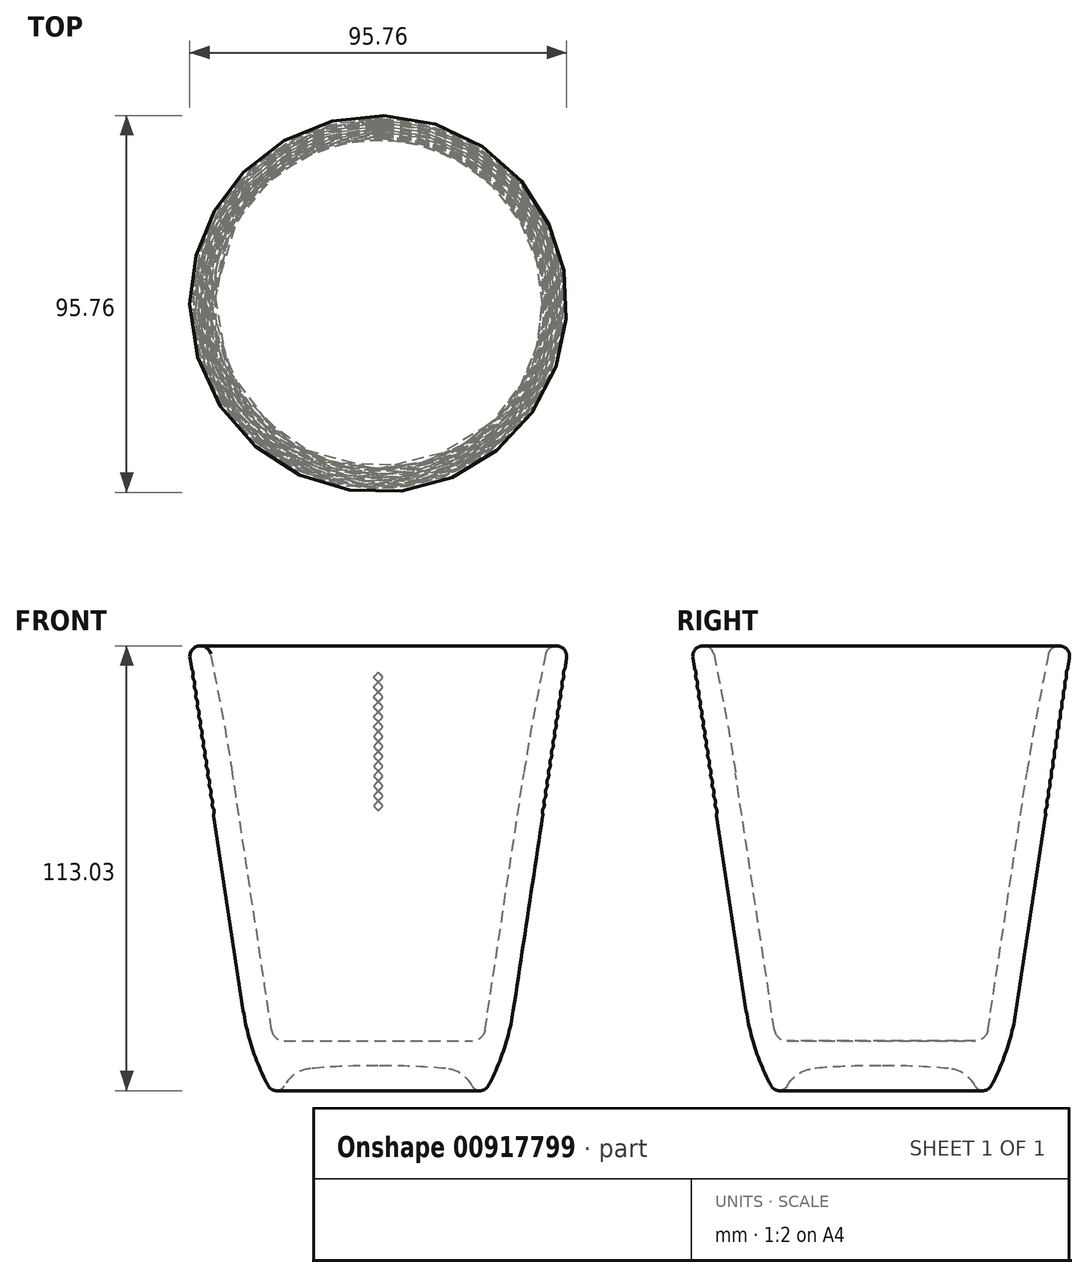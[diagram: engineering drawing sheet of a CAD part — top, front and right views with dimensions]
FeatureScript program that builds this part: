
annotation { "Feature Type Name" : "Feature", "Feature Type Description" : "" }
export const myFeature = defineFeature(function(context is Context, id is Id, definition is map)
    precondition{}
    {
        {
            var Q0;
            Q0=qCreatedBy(makeId("Right.planeOp"),FACE);
            var sketch = newSketch(context, id + "F0", { "sketchPlane" : qUnion([Q0])});
            skLineSegment(sketch, "E0", {"start": v(0, 0) * mm, "end": v(0, 6.35) * mm, "construction": true});
            skArc(sketch, "E1", {"start": v(0, 6.35) * mm, "mid": v(-8.58, 6.17) * mm, "end": v(-17.15, 5.63) * mm});
            skLineSegment(sketch, "E2", {"start": v(-47.85, 109.92) * mm, "end": v(-31.21, 0) * mm});
            skLineSegment(sketch, "E3", {"start": v(-31.21, 0) * mm, "end": v(0, 0) * mm, "construction": true});
            skArc(sketch, "E4", {"start": v(-17.15, 5.63) * mm, "mid": v(-21.07, 4.27) * mm, "end": v(-23.88, 1.2) * mm});
            skArc(sketch, "E5", {"start": v(-27.92, 1.2) * mm, "mid": v(-25.9, 0) * mm, "end": v(-23.88, 1.2) * mm});
            skArc(sketch, "E6", {"start": v(-34.3, 20.32) * mm, "mid": v(-31.93, 10.5) * mm, "end": v(-27.92, 1.2) * mm});
            skLineSegment(sketch, "E7", {"start": v(0, 6.35) * mm, "end": v(0, 12.7) * mm});
            skLineSegment(sketch, "E8", {"start": v(0, 12.7) * mm, "end": v(0, 113.03) * mm, "construction": true});
            skLineSegment(sketch, "E9", {"start": v(0, 12.7) * mm, "end": v(-23.98, 12.7) * mm});
            skArc(sketch, "E10", {"start": v(-27.12, 15.4) * mm, "mid": v(-26.05, 13.47) * mm, "end": v(-23.98, 12.7) * mm});
            skLineSegment(sketch, "E11", {"start": v(-27.12, 15.4) * mm, "end": v(-37, 80.64) * mm});
            skArc(sketch, "E12", {"start": v(-42.54, 110.9) * mm, "mid": v(-45.66, 112.99) * mm, "end": v(-47.85, 109.92) * mm});
            skArc(sketch, "E13", {"start": v(-37, 80.64) * mm, "mid": v(-39.53, 95.81) * mm, "end": v(-42.54, 110.9) * mm});
            skLineSegment(sketch, "E14", {"start": v(-45.18, 113.03) * mm, "end": v(0, 113.03) * mm, "construction": true});
            skLineSegment(sketch, "E15", {"start": v(-47.88, 110.33) * mm, "end": v(-47.88, 115.02) * mm, "construction": true});
            skPoint(sketch, "E16", {"position": v(0, 69.85) * mm});
            skLineSegment(sketch, "E17", {"start": v(-47.85, 109.92) * mm, "end": v(0, 109.92) * mm, "construction": true});
            skSolve(sketch);
        }
        {
            var Q0;
            Q0 = qSketchRegion(id + "F0", true);
            var Q1;
            Q1=sQuery(id+"F0.wireOp",EDGE,"E7");
            revolve(context, id + "F1", {"surfaceOperationType" : NewSurfaceOperationType.NEW, "entities" : qUnion([Q0]), "axis" : qUnion([Q1]), "revolveType" : RevolveType.FULL});
        }
        {
            var Q0;
            Q0=qCreatedBy(makeId("Top.planeOp"),FACE);
            var Q1;
            Q1=sQuery(id+"F0.wireOp",VERTEX,"E16");
            cPlane(context, id + "F2", {"entities" : qUnion([Q0, Q1]), "cplaneType" : CPlaneType.PLANE_POINT, "offset" : 25.4 * mm, "width" : 152.4 * mm, "height" : 152.4 * mm});
        }
        {
            var Q0;
            Q0=qCreatedBy(id+"F2.planeOp",FACE);
            var sketch = newSketch(context, id + "F3", { "sketchPlane" : qUnion([Q0])});
            skCircle(sketch, "E18.cCircle", {"center": v(0, 0) * mm, "radius": 35.98 * mm, "construction": true});
            skLineSegment(sketch, "E18.0", {"start": v(0, 39.94) * mm, "end": v(31.23, 24.9) * mm});
            skLineSegment(sketch, "E18.1", {"start": v(31.23, 24.9) * mm, "end": v(38.94, -8.89) * mm});
            skLineSegment(sketch, "E18.2", {"start": v(38.94, -8.89) * mm, "end": v(17.33, -35.98) * mm});
            skLineSegment(sketch, "E18.3", {"start": v(17.33, -35.98) * mm, "end": v(-17.33, -35.98) * mm});
            skLineSegment(sketch, "E18.4", {"start": v(-17.33, -35.98) * mm, "end": v(-38.94, -8.89) * mm});
            skLineSegment(sketch, "E18.5", {"start": v(-38.94, -8.89) * mm, "end": v(-31.23, 24.9) * mm});
            skLineSegment(sketch, "E18.6", {"start": v(-31.23, 24.9) * mm, "end": v(0, 39.94) * mm});
            skPoint(sketch, "E18.0.midPoint", {"position": v(15.61, 32.42) * mm});
            skLineSegment(sketch, "E19", {"start": v(0, 0) * mm, "end": v(0, 39.94) * mm, "construction": true});
            skLineSegment(sketch, "E20", {"start": v(17.33, -35.98) * mm, "end": v(0, 0) * mm, "construction": true});
            skLineSegment(sketch, "E21", {"start": v(-17.33, -35.98) * mm, "end": v(0, 0) * mm, "construction": true});
            skSolve(sketch);
        }
        {
            var Q0;
            Q0=qCreatedBy(makeId("Right.planeOp"),FACE);
            var sketch = newSketch(context, id + "F4", { "sketchPlane" : qUnion([Q0])});
            skLineSegment(sketch, "E22", {"start": v(47.85, 109.92) * mm, "end": v(34.3, 20.32) * mm, "construction": true});
            skLineSegment(sketch, "E23", {"start": v(39.94, 69.85) * mm, "end": v(41.78, 69.85) * mm, "construction": true});
            skArc(sketch, "E24", {"start": v(41.78, 69.85) * mm, "mid": v(41.8, 70.17) * mm, "end": v(41.75, 70.5) * mm});
            skArc(sketch, "E25", {"start": v(41.94, 71.75) * mm, "mid": v(41.72, 71.14) * mm, "end": v(41.75, 70.5) * mm});
            skArc(sketch, "E26", {"start": v(41.94, 71.75) * mm, "mid": v(42.08, 72.05) * mm, "end": v(42.16, 72.36) * mm});
            skLineSegment(sketch, "E27", {"start": v(41.75, 70.5) * mm, "end": v(41.94, 71.75) * mm, "construction": true});
            skLineSegment(sketch, "E28", {"start": v(41.72, 71.14) * mm, "end": v(41.97, 71.1) * mm, "construction": true});
            skLineSegment(sketch, "E29", {"start": v(41.78, 69.85) * mm, "end": v(42.16, 72.36) * mm});
            skArc(sketch, "E30.1.0.0", {"start": v(42.32, 74.26) * mm, "mid": v(42.46, 74.56) * mm, "end": v(42.54, 74.87) * mm});
            skArc(sketch, "E30.1.0.1", {"start": v(42.32, 74.26) * mm, "mid": v(42.1, 73.66) * mm, "end": v(42.13, 73) * mm});
            skArc(sketch, "E30.1.0.2", {"start": v(42.16, 72.36) * mm, "mid": v(42.18, 72.69) * mm, "end": v(42.13, 73) * mm});
            skLineSegment(sketch, "E30.1.0.3", {"start": v(42.16, 72.36) * mm, "end": v(42.54, 74.87) * mm});
            skArc(sketch, "E30.2.0.0", {"start": v(42.7, 76.78) * mm, "mid": v(42.84, 77.07) * mm, "end": v(42.92, 77.38) * mm});
            skArc(sketch, "E30.2.0.1", {"start": v(42.7, 76.78) * mm, "mid": v(42.48, 76.17) * mm, "end": v(42.51, 75.52) * mm});
            skArc(sketch, "E30.2.0.2", {"start": v(42.54, 74.87) * mm, "mid": v(42.56, 75.2) * mm, "end": v(42.51, 75.52) * mm});
            skLineSegment(sketch, "E30.2.0.3", {"start": v(42.54, 74.87) * mm, "end": v(42.92, 77.38) * mm});
            skArc(sketch, "E30.3.0.0", {"start": v(43.08, 79.29) * mm, "mid": v(43.22, 79.58) * mm, "end": v(43.3, 79.9) * mm});
            skArc(sketch, "E30.3.0.1", {"start": v(43.08, 79.29) * mm, "mid": v(42.86, 78.68) * mm, "end": v(42.9, 78.03) * mm});
            skArc(sketch, "E30.3.0.2", {"start": v(42.92, 77.38) * mm, "mid": v(42.94, 77.7) * mm, "end": v(42.9, 78.03) * mm});
            skLineSegment(sketch, "E30.3.0.3", {"start": v(42.92, 77.38) * mm, "end": v(43.3, 79.9) * mm});
            skArc(sketch, "E30.4.0.0", {"start": v(43.46, 81.8) * mm, "mid": v(43.6, 82.1) * mm, "end": v(43.68, 82.4) * mm});
            skArc(sketch, "E30.4.0.1", {"start": v(43.46, 81.8) * mm, "mid": v(43.24, 81.19) * mm, "end": v(43.27, 80.54) * mm});
            skArc(sketch, "E30.4.0.2", {"start": v(43.3, 79.9) * mm, "mid": v(43.32, 80.22) * mm, "end": v(43.27, 80.54) * mm});
            skLineSegment(sketch, "E30.4.0.3", {"start": v(43.3, 79.9) * mm, "end": v(43.68, 82.4) * mm});
            skArc(sketch, "E30.5.0.0", {"start": v(43.84, 84.3) * mm, "mid": v(43.98, 84.6) * mm, "end": v(44.06, 84.92) * mm});
            skArc(sketch, "E30.5.0.1", {"start": v(43.84, 84.3) * mm, "mid": v(43.62, 83.7) * mm, "end": v(43.65, 83.05) * mm});
            skArc(sketch, "E30.5.0.2", {"start": v(43.68, 82.4) * mm, "mid": v(43.7, 82.73) * mm, "end": v(43.65, 83.05) * mm});
            skLineSegment(sketch, "E30.5.0.3", {"start": v(43.68, 82.4) * mm, "end": v(44.06, 84.92) * mm});
            skArc(sketch, "E30.6.0.0", {"start": v(44.22, 86.82) * mm, "mid": v(44.36, 87.11) * mm, "end": v(44.44, 87.43) * mm});
            skArc(sketch, "E30.6.0.1", {"start": v(44.22, 86.82) * mm, "mid": v(44, 86.21) * mm, "end": v(44.03, 85.57) * mm});
            skArc(sketch, "E30.6.0.2", {"start": v(44.06, 84.92) * mm, "mid": v(44.08, 85.24) * mm, "end": v(44.03, 85.57) * mm});
            skLineSegment(sketch, "E30.6.0.3", {"start": v(44.06, 84.92) * mm, "end": v(44.44, 87.43) * mm});
            skArc(sketch, "E30.7.0.0", {"start": v(44.6, 89.33) * mm, "mid": v(44.74, 89.63) * mm, "end": v(44.82, 89.94) * mm});
            skArc(sketch, "E30.7.0.1", {"start": v(44.6, 89.33) * mm, "mid": v(44.38, 88.72) * mm, "end": v(44.41, 88.08) * mm});
            skArc(sketch, "E30.7.0.2", {"start": v(44.44, 87.43) * mm, "mid": v(44.46, 87.75) * mm, "end": v(44.41, 88.08) * mm});
            skLineSegment(sketch, "E30.7.0.3", {"start": v(44.44, 87.43) * mm, "end": v(44.82, 89.94) * mm});
            skArc(sketch, "E30.8.0.0", {"start": v(44.98, 91.84) * mm, "mid": v(45.12, 92.14) * mm, "end": v(45.2, 92.45) * mm});
            skArc(sketch, "E30.8.0.1", {"start": v(44.98, 91.84) * mm, "mid": v(44.76, 91.23) * mm, "end": v(44.8, 90.59) * mm});
            skArc(sketch, "E30.8.0.2", {"start": v(44.82, 89.94) * mm, "mid": v(44.84, 90.27) * mm, "end": v(44.8, 90.59) * mm});
            skLineSegment(sketch, "E30.8.0.3", {"start": v(44.82, 89.94) * mm, "end": v(45.2, 92.45) * mm});
            skArc(sketch, "E30.9.0.0", {"start": v(45.36, 94.36) * mm, "mid": v(45.5, 94.65) * mm, "end": v(45.58, 94.96) * mm});
            skArc(sketch, "E30.9.0.1", {"start": v(45.36, 94.36) * mm, "mid": v(45.14, 93.75) * mm, "end": v(45.17, 93.1) * mm});
            skArc(sketch, "E30.9.0.2", {"start": v(45.2, 92.45) * mm, "mid": v(45.22, 92.78) * mm, "end": v(45.17, 93.1) * mm});
            skLineSegment(sketch, "E30.9.0.3", {"start": v(45.2, 92.45) * mm, "end": v(45.58, 94.96) * mm});
            skArc(sketch, "E30.10.0.0", {"start": v(45.74, 96.87) * mm, "mid": v(45.88, 97.16) * mm, "end": v(45.96, 97.48) * mm});
            skArc(sketch, "E30.10.0.1", {"start": v(45.74, 96.87) * mm, "mid": v(45.52, 96.26) * mm, "end": v(45.55, 95.61) * mm});
            skArc(sketch, "E30.10.0.2", {"start": v(45.58, 94.96) * mm, "mid": v(45.6, 95.29) * mm, "end": v(45.55, 95.61) * mm});
            skLineSegment(sketch, "E30.10.0.3", {"start": v(45.58, 94.96) * mm, "end": v(45.96, 97.48) * mm});
            skArc(sketch, "E30.11.0.0", {"start": v(46.12, 99.38) * mm, "mid": v(46.26, 99.67) * mm, "end": v(46.34, 99.99) * mm});
            skArc(sketch, "E30.11.0.1", {"start": v(46.12, 99.38) * mm, "mid": v(45.9, 98.77) * mm, "end": v(45.93, 98.12) * mm});
            skArc(sketch, "E30.11.0.2", {"start": v(45.96, 97.48) * mm, "mid": v(45.98, 97.8) * mm, "end": v(45.93, 98.12) * mm});
            skLineSegment(sketch, "E30.11.0.3", {"start": v(45.96, 97.48) * mm, "end": v(46.34, 99.99) * mm});
            skArc(sketch, "E30.12.0.0", {"start": v(46.5, 101.89) * mm, "mid": v(46.64, 102.18) * mm, "end": v(46.72, 102.5) * mm});
            skArc(sketch, "E30.12.0.1", {"start": v(46.5, 101.89) * mm, "mid": v(46.28, 101.28) * mm, "end": v(46.31, 100.63) * mm});
            skArc(sketch, "E30.12.0.2", {"start": v(46.34, 99.99) * mm, "mid": v(46.36, 100.31) * mm, "end": v(46.31, 100.63) * mm});
            skLineSegment(sketch, "E30.12.0.3", {"start": v(46.34, 99.99) * mm, "end": v(46.72, 102.5) * mm});
            skArc(sketch, "E30.13.0.0", {"start": v(46.88, 104.4) * mm, "mid": v(47.02, 104.7) * mm, "end": v(47.1, 105) * mm});
            skArc(sketch, "E30.13.0.1", {"start": v(46.88, 104.4) * mm, "mid": v(46.66, 103.8) * mm, "end": v(46.7, 103.15) * mm});
            skArc(sketch, "E30.13.0.2", {"start": v(46.72, 102.5) * mm, "mid": v(46.74, 102.82) * mm, "end": v(46.7, 103.15) * mm});
            skLineSegment(sketch, "E30.13.0.3", {"start": v(46.72, 102.5) * mm, "end": v(47.1, 105) * mm});
            skArc(sketch, "E30.14.0.0", {"start": v(47.26, 106.91) * mm, "mid": v(47.4, 107.2) * mm, "end": v(47.48, 107.52) * mm});
            skArc(sketch, "E30.14.0.1", {"start": v(47.26, 106.91) * mm, "mid": v(47.04, 106.3) * mm, "end": v(47.07, 105.66) * mm});
            skArc(sketch, "E30.14.0.2", {"start": v(47.1, 105) * mm, "mid": v(47.12, 105.33) * mm, "end": v(47.07, 105.66) * mm});
            skLineSegment(sketch, "E30.14.0.3", {"start": v(47.1, 105) * mm, "end": v(47.48, 107.52) * mm});
            skLineSegment(sketch, "E30.direction1", {"start": v(41.94, 71.75) * mm, "end": v(42.32, 74.26) * mm, "construction": true});
            skPoint(sketch, "E31", {"position": v(47.3, 106.27) * mm});
            skSolve(sketch);
        }
        {
            var Q0;
            Q0 = qSketchRegion(id + "F4", true);
            var Q1;
            Q1=sQuery(id+"F0.wireOp",EDGE,"E8");
            revolve(context, id + "F5", {"operationType" : NewBodyOperationType.REMOVE, "surfaceOperationType" : NewSurfaceOperationType.NEW, "entities" : qUnion([Q0]), "axis" : qUnion([Q1]), "revolveType" : RevolveType.FULL, "oppositeDirection" : true});
        }
        {
            var Q0;
            Q0=sQuery(id+"F4.wireOp",EDGE,"E29");
            cPoint(context, id + "F6", {"entities" : qUnion([Q0]), "parameter" : 0.5});
        }
        {
            var Q0;
            Q0=sQuery(id+"F4.wireOp",EDGE,"E29");
            var Q1;
            Q1 = qCreatedBy(id + "F6" ,VERTEX);
            cPlane(context, id + "F7", {"entities" : qUnion([Q0, Q1]), "cplaneType" : CPlaneType.LINE_POINT, "offset" : 25.4 * mm, "width" : 152.4 * mm, "height" : 152.4 * mm});
        }
        {
            var Q0;
            Q0=qCreatedBy(id+"F7.planeOp",FACE);
            var sketch = newSketch(context, id + "F8", { "sketchPlane" : qUnion([Q0])});
            skArc(sketch, "E32", {"start": v(-0.63, 30.74) * mm, "mid": v(0, 30.6) * mm, "end": v(0.63, 30.74) * mm});
            skArc(sketch, "E33", {"start": v(-0.63, 30.74) * mm, "mid": v(-0.95, 30.83) * mm, "end": v(-1.27, 30.86) * mm});
            skArc(sketch, "E34", {"start": v(1.27, 30.86) * mm, "mid": v(0.95, 30.83) * mm, "end": v(0.63, 30.74) * mm});
            skPoint(sketch, "E35.0", {"position": v(0, 30.86) * mm});
            skLineSegment(sketch, "E36", {"start": v(1.27, 30.86) * mm, "end": v(-1.27, 30.86) * mm});
            skLineSegment(sketch, "E37", {"start": v(0, 30.6) * mm, "end": v(0, 30.86) * mm, "construction": true});
            skSolve(sketch);
        }
        {
            var Q0;
            Q0=makeQuery(id+"F8.imprint","IMPRINT",FACE,{"disambiguationData":[TD([[makeQuery(id+"F8.imprint","IMPRINT",EDGE,{"derivedFrom":sQuery(id+"F8.wireOp",EDGE,"E32")}),1.0]])]});
            var Q1;
            Q1=sQuery(id+"F4.wireOp",VERTEX,"E31");
            extrude(context, id + "F9", {"entities" : qUnion([Q0]), "operationType" : NewBodyOperationType.REMOVE, "endBound" : BoundingType.UP_TO_VERTEX, "depth" : 25.4 * mm, "endBoundEntityVertex" : qUnion([Q1]), "offsetDistance" : 25.4 * mm});
        }
    });
